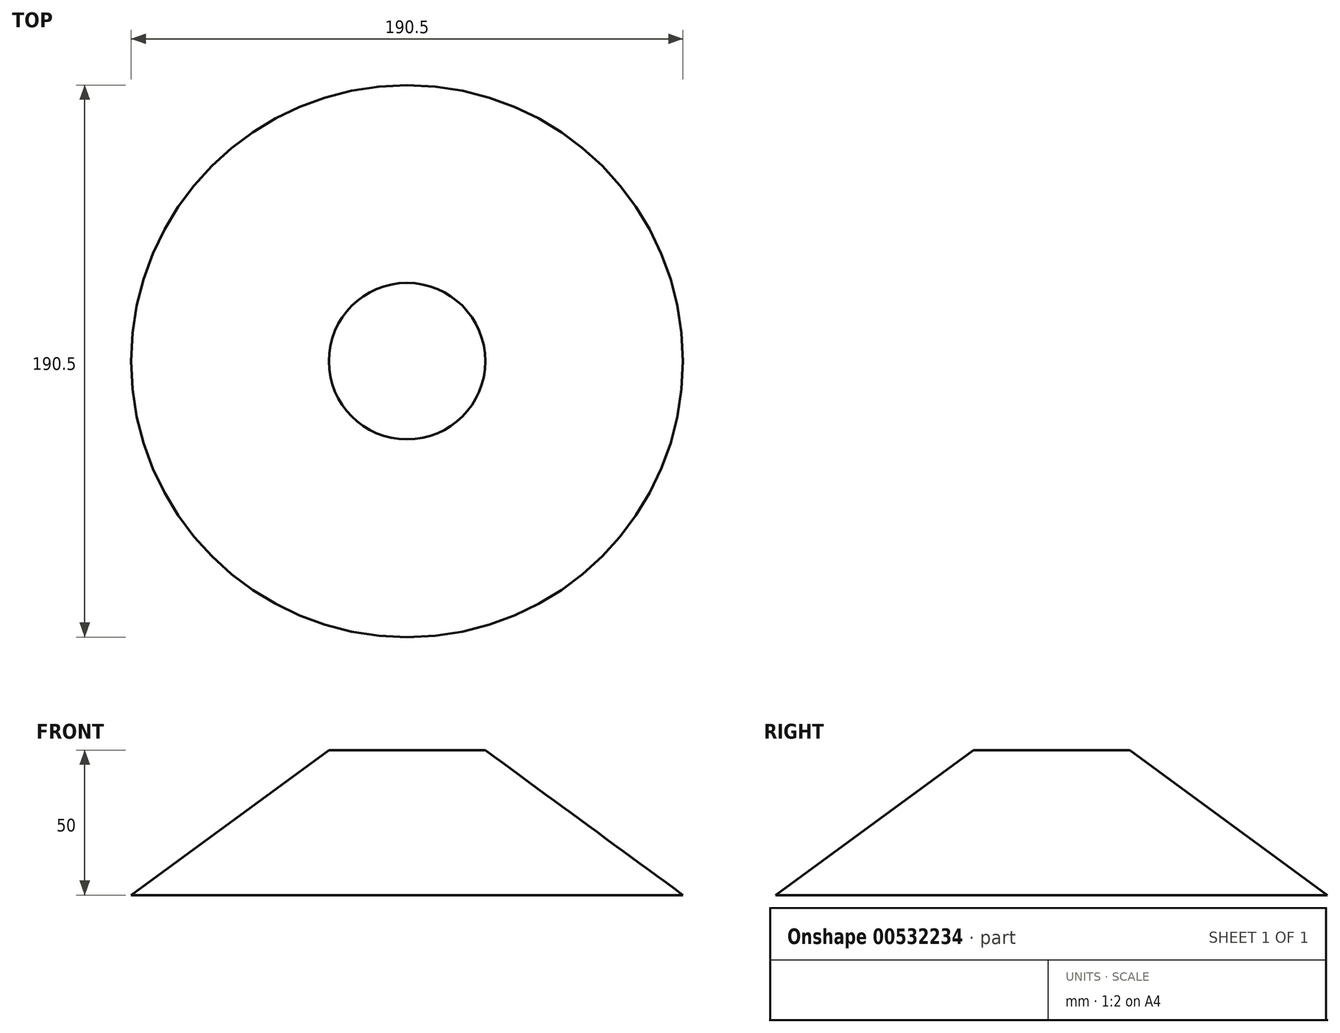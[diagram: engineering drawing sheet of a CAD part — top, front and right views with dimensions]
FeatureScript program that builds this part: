
annotation { "Feature Type Name" : "Feature", "Feature Type Description" : "" }
export const myFeature = defineFeature(function(context is Context, id is Id, definition is map)
    precondition{}
    {
        {
            var Q0;
            Q0=qCreatedBy(makeId("Top.planeOp"),FACE);
            var sketch = newSketch(context, id + "F0", { "sketchPlane" : qUnion([Q0])});
            skCircle(sketch, "E0", {"center": v(0, 0) * mm, "radius": 95.25 * mm});
            skSolve(sketch);
        }
        {
            var Q0;
            Q0=qCreatedBy(makeId("Top.planeOp"),FACE);
            cPlane(context, id + "F1", {"entities" : qUnion([Q0]), "cplaneType" : CPlaneType.OFFSET, "offset" : 50 * mm, "width" : 150 * mm, "height" : 150 * mm});
        }
        {
            var Q0;
            Q0=qCreatedBy(id+"F1.planeOp",FACE);
            var sketch = newSketch(context, id + "F2", { "sketchPlane" : qUnion([Q0])});
            skCircle(sketch, "E1", {"center": v(0, 0) * mm, "radius": 27 * mm});
            skSolve(sketch);
        }
        {
            var Q0;
            Q0=makeQuery(id+"F0.imprint","IMPRINT",FACE,{"disambiguationData":[TD([[makeQuery(id+"F0.imprint","IMPRINT",EDGE,{"derivedFrom":sQuery(id+"F0.wireOp",EDGE,"E0")}),1.0]])]});
            var Q1;
            Q1=makeQuery(id+"F2.imprint","IMPRINT",FACE,{"disambiguationData":[TD([[makeQuery(id+"F2.imprint","IMPRINT",EDGE,{"derivedFrom":sQuery(id+"F2.wireOp",EDGE,"E1")}),1.0]])]});
            loft(context, id + "F3", {"sheetProfilesArray" : [{ "sheetProfileEntities" : qUnion([Q0]) }, { "sheetProfileEntities" : qUnion([Q1]) }]});
        }
    });
